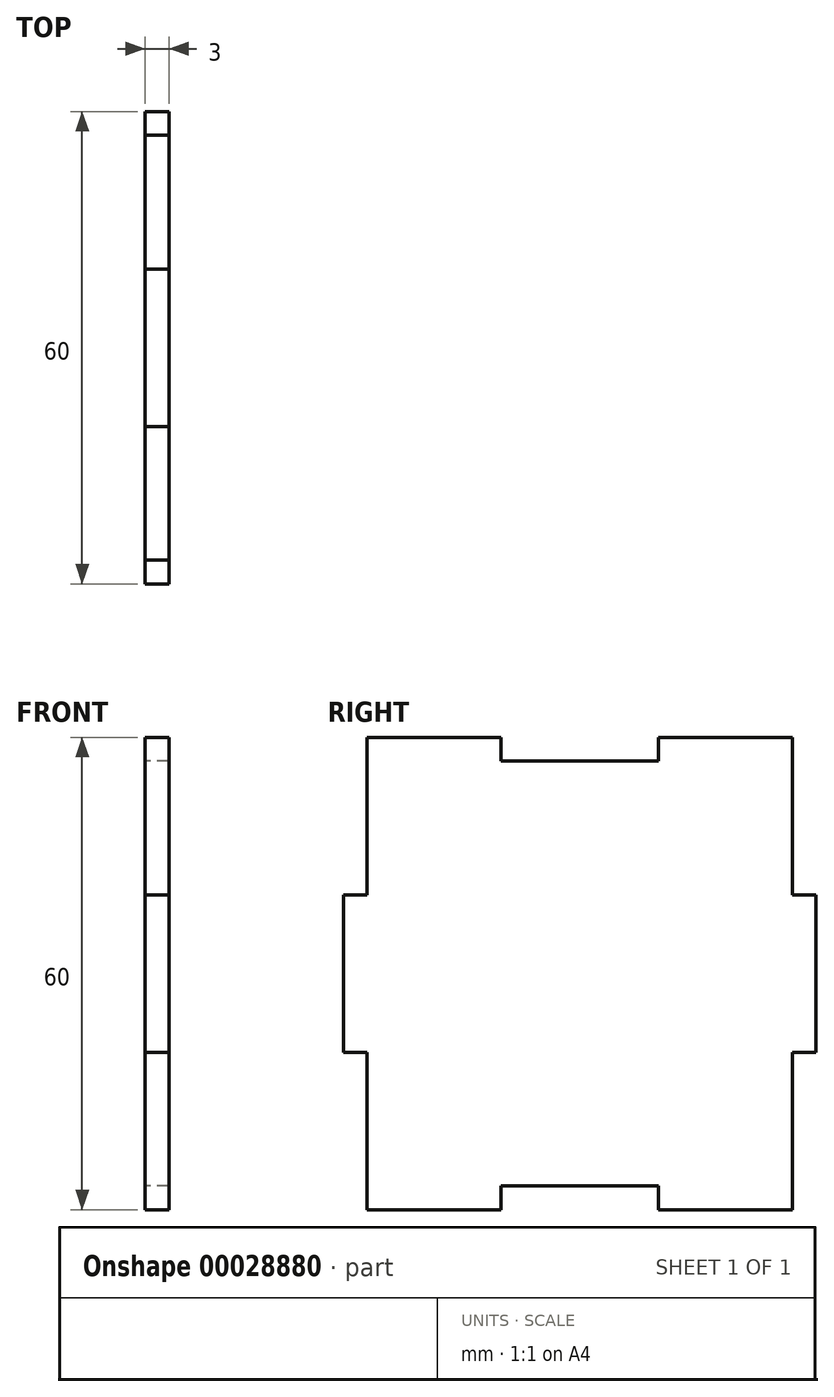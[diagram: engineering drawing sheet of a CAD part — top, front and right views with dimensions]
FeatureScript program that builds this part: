
annotation { "Feature Type Name" : "Feature", "Feature Type Description" : "" }
export const myFeature = defineFeature(function(context is Context, id is Id, definition is map)
    precondition{}
    {
        {
            var Q0;
            Q0=qCreatedBy(makeId("Right.planeOp"),FACE);
            var sketch = newSketch(context, id + "F0", { "sketchPlane" : qUnion([Q0])});
            skLineSegment(sketch, "E0", {"start": v(-30, 0) * mm, "end": v(-30, 10) * mm});
            skLineSegment(sketch, "E1", {"start": v(-30, 10) * mm, "end": v(-27, 10) * mm});
            skLineSegment(sketch, "E2", {"start": v(-27, 10) * mm, "end": v(-27, 30) * mm});
            skLineSegment(sketch, "E3", {"start": v(-27, 30) * mm, "end": v(-10, 30) * mm});
            skLineSegment(sketch, "E4", {"start": v(-10, 30) * mm, "end": v(-10, 27) * mm});
            skLineSegment(sketch, "E5", {"start": v(-10, 27) * mm, "end": v(0, 27) * mm});
            skLineSegment(sketch, "E6.MirrorCS", {"start": v(30, 10) * mm, "end": v(27, 10) * mm});
            skLineSegment(sketch, "E7.MirrorCS", {"start": v(10, 30) * mm, "end": v(10, 27) * mm});
            skLineSegment(sketch, "E8.MirrorCS", {"start": v(27, 10) * mm, "end": v(27, 30) * mm});
            skLineSegment(sketch, "E9.MirrorCS", {"start": v(30, 0) * mm, "end": v(30, 10) * mm});
            skLineSegment(sketch, "E10.MirrorCS", {"start": v(27, 30) * mm, "end": v(10, 30) * mm});
            skLineSegment(sketch, "E11.MirrorCS", {"start": v(10, 27) * mm, "end": v(0, 27) * mm});
            skLineSegment(sketch, "E12.MirrorCS", {"start": v(-30, -10) * mm, "end": v(-27, -10) * mm});
            skLineSegment(sketch, "E13.MirrorCS", {"start": v(30, -10) * mm, "end": v(27, -10) * mm});
            skLineSegment(sketch, "E14.MirrorCS", {"start": v(-10, -30) * mm, "end": v(-10, -27) * mm});
            skLineSegment(sketch, "E15.MirrorCS", {"start": v(-27, -30) * mm, "end": v(-10, -30) * mm});
            skLineSegment(sketch, "E16.MirrorCS", {"start": v(-10, -27) * mm, "end": v(0, -27) * mm});
            skLineSegment(sketch, "E17.MirrorCS", {"start": v(-30, 0) * mm, "end": v(-30, -10) * mm});
            skLineSegment(sketch, "E18.MirrorCS", {"start": v(-27, -10) * mm, "end": v(-27, -30) * mm});
            skLineSegment(sketch, "E19.MirrorCS", {"start": v(10, -30) * mm, "end": v(10, -27) * mm});
            skLineSegment(sketch, "E20.MirrorCS", {"start": v(27, -10) * mm, "end": v(27, -30) * mm});
            skLineSegment(sketch, "E21.MirrorCS", {"start": v(10, -27) * mm, "end": v(0, -27) * mm});
            skLineSegment(sketch, "E22.MirrorCS", {"start": v(27, -30) * mm, "end": v(10, -30) * mm});
            skLineSegment(sketch, "E23.MirrorCS", {"start": v(30, 0) * mm, "end": v(30, -10) * mm});
            skSolve(sketch);
        }
        {
            var Q0;
            Q0=makeQuery(id+"F0.imprint","IMPRINT",FACE,{"disambiguationData":[TD([[makeQuery(id+"F0.imprint","IMPRINT",EDGE,{"derivedFrom":sQuery(id+"F0.wireOp",EDGE,"E0")}),-1.0]])]});
            extrude(context, id + "F1", {"entities" : qUnion([Q0]), "depth" : 3 * mm});
        }
    });
